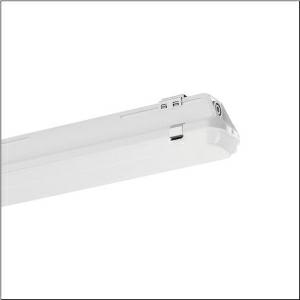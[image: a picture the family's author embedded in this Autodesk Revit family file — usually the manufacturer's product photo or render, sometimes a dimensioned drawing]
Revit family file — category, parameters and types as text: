
# Revit family: monsun_r__12_51fp10dp460h_b3d6
name_source: partatom
category: Lighting Fixtures
units: mm (PartAtom-declared; Revit-internal decimal feet)

## family parameters
Cut with Voids When Loaded = No
Host = Face
Light Source = No
Part Type = Normal
Room Calculation Point = No
Round Connector Dimension = Use Diameter
Shared = No

## types (1)
- --- (1 x LED, 6050 lm, 34.6 W, 4000K)
    Apparent Load = 35 VA
    CIE Flux Codes = 47 77 93 94 100
    Color Rendering = 80
    Color Temperature = 4000K
    Default Elevation = 1800 mm
    Description = Monsun® 12, damp-proof luminaire, chain hanger, primary optical cover: enclosure, of PMMA, light emission: direct distribution, primary light characteristic: symmetric, installation type: suspended mounting, surface-mounted, horizontal mounting, vertical mounting, LED rated luminous flux: 6.050 lm, light colour: 840, colour temperature: 4000K, control gear: ECG DALI, with terminal, 5-pole, max. 2.5mm², mains connection: 220..240V, AC, 50/60Hz, rated input power: 35W, luminaire housing, of glass-fibre reinforced polyester, uncoated, bright grey, length: 1.590 mm, width: 90 mm, height: 88mm, clip for enclosure, of stainless steel (V2A), ceiling mounting element, of stainless steel (V2A), chain hanger, of stainless steel (V2A), protection rating (complete): IP66, insulation class (complete): insulation class I (protective earthing), certification: CE, ENEC, VDE, protection symbol: D, impact resistance: IK04, permissible ambient temperature for indoor applications: -25..+40°C, standard: EN 50419, EN 60598-2-1, no direct snow, no direct sun, no direct rain, for indoor or canopied outdoor use, corresponds to IFS (International Featured Standards) requirements for safety and quality in the food industry, for animal farming (ammonia tested): for use in cowhouse, pig house, horse-stables... (not for use in poultry stables), AT max for animal farming = 40°C, packaging unit: 1 piece
    Height = 89 mm
    Lamp = 1 x LED
    Lamp Light Flux = 6050 lm
    Lamp Power = 34.6 W
    Lamp count = 1
    Length = 1590 mm
    Luminous efficacy = 175 lm/W
    Manufacturer = Siteco
    ModVariant = No
    Model = 51FP10DP460H
    Mounting Place = Ceiling
    Mounting Type = Pendant
    Number of Poles = 1
    OnlyDefault = Yes
    Power Factor = 1
    Product Name = Monsun® 12
    Product group = damp-proof luminaire | ceiling pendant
    ProductGroupID = 908
    Protection Class = Protection class I
    Protection Degree = IP 66
    RLX_Detail_Level = 1
    RlxData = <blob elided: 92237 chars, md5=e6b3af67>
    Socket = socket
    Standby Power = 0 W
    System Light Flux = 6050 lm
    System Power = 35 W
    Type Comments = factory setting: luminous flux: 100 % | dim-lin: 254 | 232 mA
    Type Image = l_1004748.jpg
    URL = http://relux.com
    VarID = @adj_136213
    Voltage = 0 V
    Weight = 0.00 kg
    Width = 90 mm

## geometry (parser evidence)
native form markers: Blend x4, Sweep x13
no freeform markers — native parametric forms only
